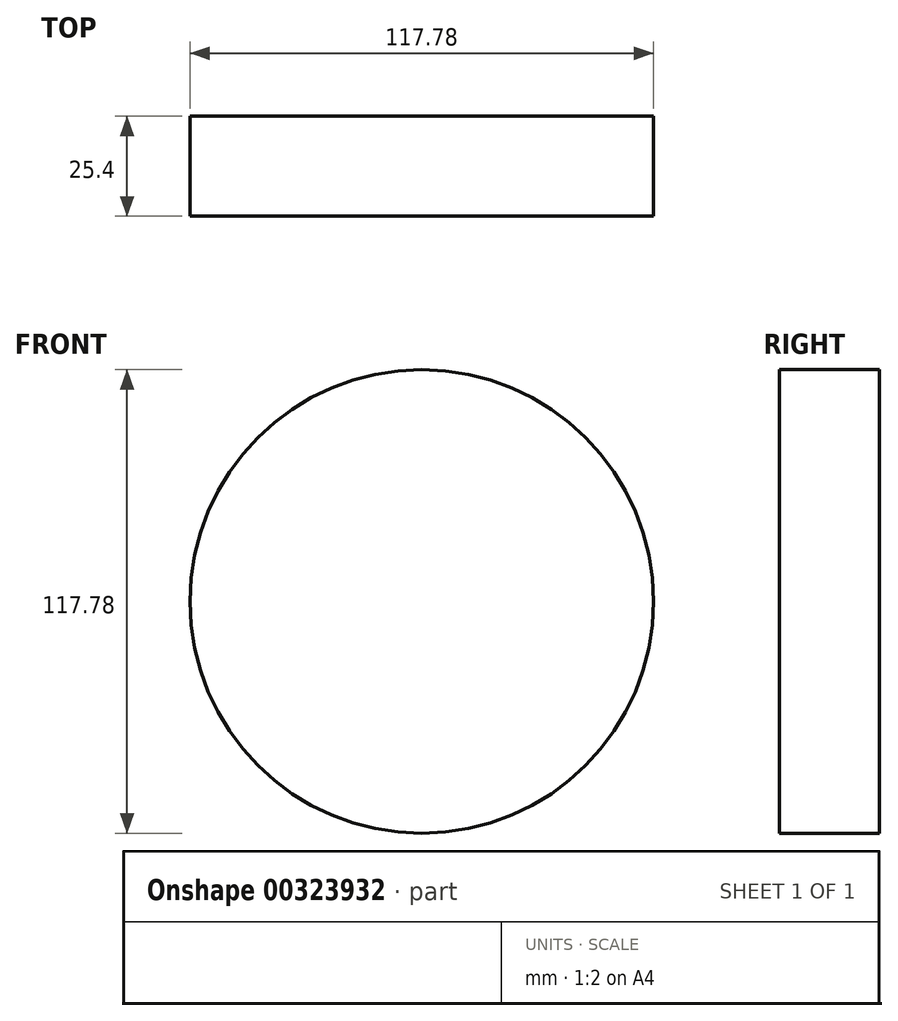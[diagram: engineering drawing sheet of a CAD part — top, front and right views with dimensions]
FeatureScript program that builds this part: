
annotation { "Feature Type Name" : "Feature", "Feature Type Description" : "" }
export const myFeature = defineFeature(function(context is Context, id is Id, definition is map)
    precondition{}
    {
        {
            var Q0;
            Q0=qCreatedBy(makeId("Front.planeOp"),FACE);
            var sketch = newSketch(context, id + "F0", { "sketchPlane" : qUnion([Q0])});
            skCircle(sketch, "E0", {"center": v(0, 0) * mm, "radius": 58.89 * mm});
            skSolve(sketch);
        }
        {
            var Q0;
            Q0 = qSketchRegion(id + "F0", true);
            extrude(context, id + "F1", {"entities" : qUnion([Q0]), "depth" : 25.4 * mm});
        }
    });
